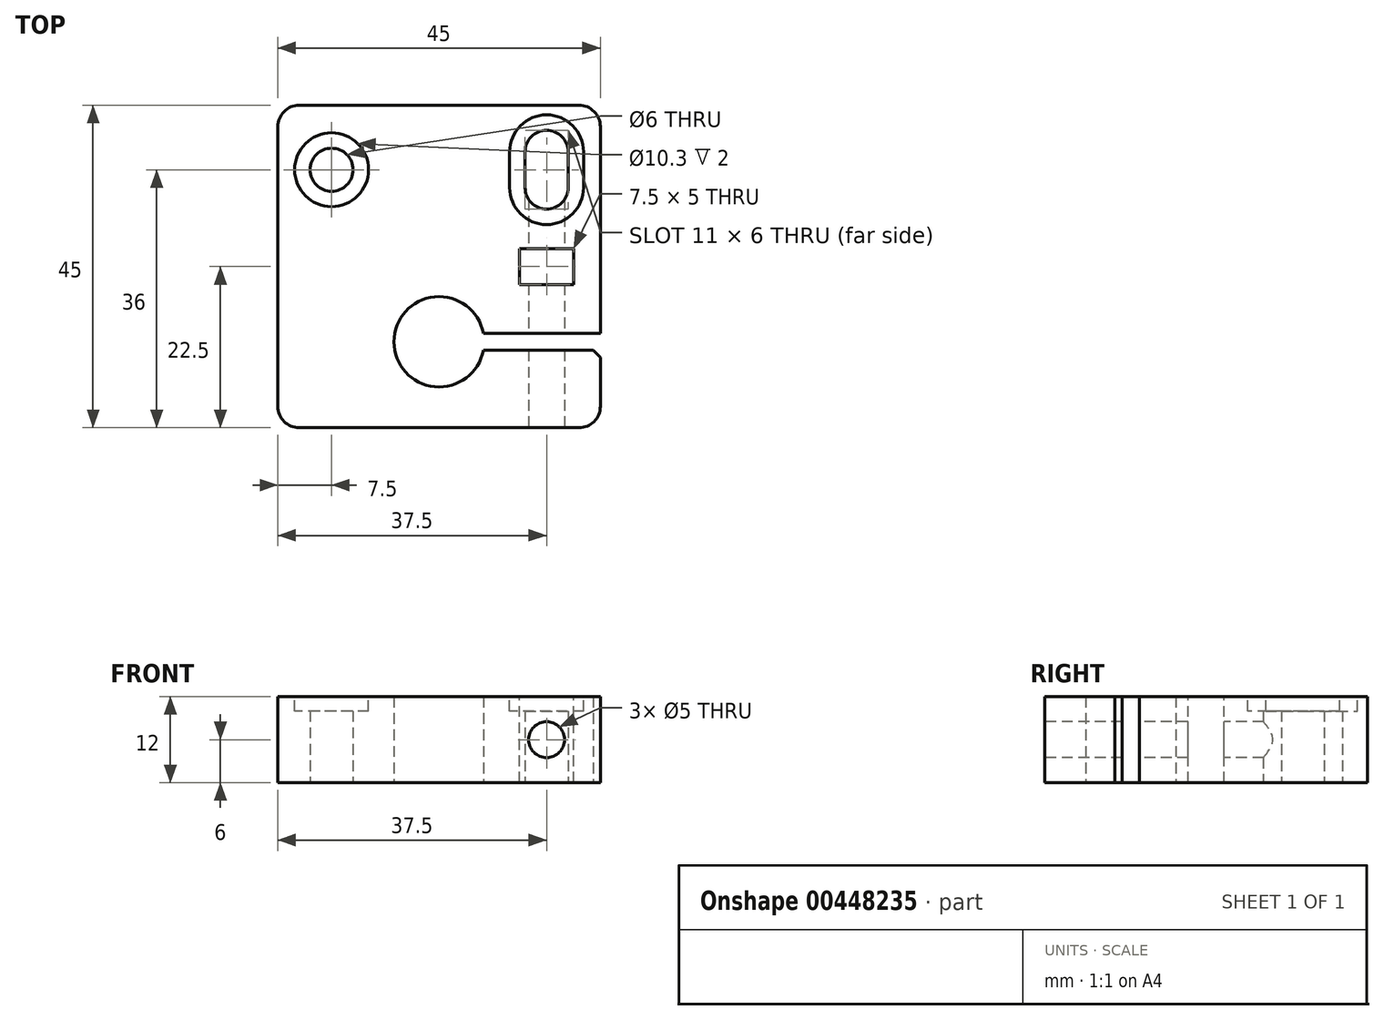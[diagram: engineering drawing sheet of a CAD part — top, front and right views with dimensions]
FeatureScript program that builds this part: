
annotation { "Feature Type Name" : "Feature", "Feature Type Description" : "" }
export const myFeature = defineFeature(function(context is Context, id is Id, definition is map)
    precondition{}
    {
        {
            var Q0;
            Q0=qCreatedBy(makeId("Top.planeOp"),FACE);
            var sketch = newSketch(context, id + "F0", { "sketchPlane" : qUnion([Q0])});
            skLineSegment(sketch, "E0.bottom", {"start": v(-22.5, 33) * mm, "end": v(22.5, 33) * mm});
            skLineSegment(sketch, "E0.top", {"start": v(-22.5, -12) * mm, "end": v(22.5, -12) * mm});
            skLineSegment(sketch, "E0.left", {"start": v(-22.5, 33) * mm, "end": v(-22.5, -12) * mm});
            skLineSegment(sketch, "E0.right", {"start": v(22.5, 33) * mm, "end": v(22.5, -12) * mm});
            skCircle(sketch, "E1", {"center": v(0, 0) * mm, "radius": 6.3 * mm});
            skLineSegment(sketch, "E2", {"start": v(12, 26.5) * mm, "end": v(12, 21.5) * mm});
            skLineSegment(sketch, "E3", {"start": v(12, 21.5) * mm, "end": v(18, 21.5) * mm});
            skLineSegment(sketch, "E4", {"start": v(18, 21.5) * mm, "end": v(18, 26.5) * mm});
            skArc(sketch, "E5", {"start": v(18, 26.5) * mm, "mid": v(15, 29.5) * mm, "end": v(12, 26.5) * mm});
            skArc(sketch, "E6", {"start": v(12, 21.5) * mm, "mid": v(15, 18.5) * mm, "end": v(18, 21.5) * mm});
            skCircle(sketch, "E7", {"center": v(-15, 24) * mm, "radius": 3 * mm});
            skSolve(sketch);
        }
        {
            var Q0;
            Q0=makeQuery(id+"F0.imprint","IMPRINT",FACE,{"disambiguationData":[TD([[makeQuery(id+"F0.imprint","IMPRINT",EDGE,{"derivedFrom":sQuery(id+"F0.wireOp",EDGE,"E0.bottom")}),-1.0]])]});
            extrude(context, id + "F1", {"entities" : qUnion([Q0]), "depth" : 12 * mm});
        }
        {
            var Q0;
            Q0=makeQuery(id+"F1.opExtrude","SWEPT_FACE",FACE,{"disambiguationData":[OSD([sQuery(id+"F0.wireOp",EDGE,"E0.top")])]});
            var sketch = newSketch(context, id + "F2", { "sketchPlane" : qUnion([Q0])});
            skPoint(sketch, "E8", {"position": v(15, 6) * mm});
            skSolve(sketch);
        }
        {
            var Q0;
            Q0=sQuery(id+"F2.wireOp",VERTEX,"E8");
            var Q1;
            Q1=makeQuery(id+"F1.opExtrude","SWEPT_BODY",BODY,{"disambiguationData":[OSD([sQuery(id+"F0.wireOp",EDGE,"E0.bottom"),sQuery(id+"F0.wireOp",EDGE,"E0.top"),sQuery(id+"F0.wireOp",EDGE,"E0.left"),sQuery(id+"F0.wireOp",EDGE,"E0.right"),sQuery(id+"F0.wireOp",EDGE,"E1"),sQuery(id+"F0.wireOp",EDGE,"E2"),sQuery(id+"F0.wireOp",EDGE,"E4"),sQuery(id+"F0.wireOp",EDGE,"E5"),sQuery(id+"F0.wireOp",EDGE,"E6"),sQuery(id+"F0.wireOp",EDGE,"E7")])]});
            hole(context, id + "F3", {"style" : HoleStyle.SIMPLE, "endStyle" : HoleEndStyle.BLIND, "holeDiameter" : 5 * mm, "holeDepth" : 32 * mm, "isTappedThrough" : true, "tappedDepth" : 12 * mm, "tapClearance" : 3, "locations" : qUnion([Q0]), "scope" : qUnion([Q1])});
        }
        {
            var Q0;
            Q0=makeQuery(id+"F1.opExtrude","CAP_FACE",FACE,{"disambiguationData":[OSD([sQuery(id+"F0.wireOp",EDGE,"E0.bottom"),sQuery(id+"F0.wireOp",EDGE,"E0.top"),sQuery(id+"F0.wireOp",EDGE,"E0.left"),sQuery(id+"F0.wireOp",EDGE,"E0.right"),sQuery(id+"F0.wireOp",EDGE,"E1"),sQuery(id+"F0.wireOp",EDGE,"E2"),sQuery(id+"F0.wireOp",EDGE,"E4"),sQuery(id+"F0.wireOp",EDGE,"E5"),sQuery(id+"F0.wireOp",EDGE,"E6"),sQuery(id+"F0.wireOp",EDGE,"E7")])],"isStart":false});
            var sketch = newSketch(context, id + "F4", { "sketchPlane" : qUnion([Q0])});
            skLineSegment(sketch, "E9.bottom", {"start": v(0, 1.2) * mm, "end": v(22.5, 1.2) * mm});
            skLineSegment(sketch, "E9.top", {"start": v(0, -1.2) * mm, "end": v(22.5, -1.2) * mm});
            skLineSegment(sketch, "E9.left", {"start": v(0, 1.2) * mm, "end": v(0, -1.2) * mm});
            skLineSegment(sketch, "E9.right", {"start": v(22.5, 1.2) * mm, "end": v(22.5, -1.2) * mm});
            skSolve(sketch);
        }
        {
            var Q0;
            {var subQ0=sQuery(id+"F4.wireOp",EDGE,"E9.right");Q0=makeQuery(id+"F4.imprint","IMPRINT",FACE,{"disambiguationData":[TD([[makeQuery(id+"F4.imprint","IMPRINT",EDGE,{"derivedFrom":subQ0}),-1.0]])]});}
            var Q1;
            {var subQ0=sQuery(id+"F4.wireOp",EDGE,"E9.left");Q1=makeQuery(id+"F4.imprint","IMPRINT",FACE,{"disambiguationData":[TD([[makeQuery(id+"F4.imprint","IMPRINT",EDGE,{"derivedFrom":subQ0}),1.0]])]});}
            extrude(context, id + "F5", {"entities" : qUnion([Q0, Q1]), "operationType" : NewBodyOperationType.REMOVE, "oppositeDirection" : true, "depth" : 25 * mm});
        }
        {
            var Q0;
            Q0=makeQuery(id+"F1.opExtrude","CAP_FACE",FACE,{"disambiguationData":[OSD([sQuery(id+"F0.wireOp",EDGE,"E0.bottom"),sQuery(id+"F0.wireOp",EDGE,"E0.top"),sQuery(id+"F0.wireOp",EDGE,"E0.left"),sQuery(id+"F0.wireOp",EDGE,"E0.right"),sQuery(id+"F0.wireOp",EDGE,"E1"),sQuery(id+"F0.wireOp",EDGE,"E2"),sQuery(id+"F0.wireOp",EDGE,"E4"),sQuery(id+"F0.wireOp",EDGE,"E5"),sQuery(id+"F0.wireOp",EDGE,"E6"),sQuery(id+"F0.wireOp",EDGE,"E7")])],"isStart":false});
            var sketch = newSketch(context, id + "F6", { "sketchPlane" : qUnion([Q0])});
            skLineSegment(sketch, "E10.bottom", {"start": v(11.25, 13) * mm, "end": v(18.75, 13) * mm});
            skLineSegment(sketch, "E10.top", {"start": v(11.25, 8) * mm, "end": v(18.75, 8) * mm});
            skLineSegment(sketch, "E10.left", {"start": v(11.25, 13) * mm, "end": v(11.25, 8) * mm});
            skLineSegment(sketch, "E10.right", {"start": v(18.75, 13) * mm, "end": v(18.75, 8) * mm});
            skPoint(sketch, "E11", {"position": v(15, 8) * mm});
            skSolve(sketch);
        }
        {
            var Q0;
            Q0=makeQuery(id+"F6.imprint","IMPRINT",FACE,{"disambiguationData":[TD([[makeQuery(id+"F6.imprint","IMPRINT",EDGE,{"derivedFrom":sQuery(id+"F6.wireOp",EDGE,"E10.bottom")}),-1.0]])]});
            extrude(context, id + "F7", {"entities" : qUnion([Q0]), "operationType" : NewBodyOperationType.REMOVE, "oppositeDirection" : true, "depth" : 25 * mm});
        }
        {
            var Q0;
            Q0=makeQuery(id+"F1.opExtrude","SWEPT_EDGE",EDGE,{"disambiguationData":[OSD([sQuery(id+"F0.wireOp",EDGE,"E0.top"),sQuery(id+"F0.wireOp",EDGE,"E0.left")])]});
            var Q1;
            Q1=makeQuery(id+"F1.opExtrude","SWEPT_EDGE",EDGE,{"disambiguationData":[OSD([sQuery(id+"F0.wireOp",EDGE,"E0.top"),sQuery(id+"F0.wireOp",EDGE,"E0.right")])]});
            var Q2;
            Q2=makeQuery(id+"F1.opExtrude","SWEPT_EDGE",EDGE,{"disambiguationData":[OSD([sQuery(id+"F0.wireOp",EDGE,"E0.bottom"),sQuery(id+"F0.wireOp",EDGE,"E0.left")])]});
            var Q3;
            Q3=makeQuery(id+"F1.opExtrude","SWEPT_EDGE",EDGE,{"disambiguationData":[OSD([sQuery(id+"F0.wireOp",EDGE,"E0.bottom"),sQuery(id+"F0.wireOp",EDGE,"E0.right")])]});
            fillet(context, id + "F8", {"entities" : qUnion([Q0, Q1, Q2, Q3]), "radius" : 3 * mm, "tangentPropagation" : true, "allowEdgeOverflow" : false});
        }
        {
            var Q0;
            Q0=makeQuery(id+"F5.boolean.opBoolean","COPY",EDGE,{"derivedFrom":makeQuery(id+"F5.opExtrude","SWEPT_EDGE",EDGE,{"disambiguationData":[OSD([sQuery(id+"F0.wireOp",EDGE,"E0.right"),sQuery(id+"F4.wireOp",EDGE,"E9.top"),sQuery(id+"F4.wireOp",EDGE,"E9.right")])]})});
            var Q1;
            Q1=makeQuery(id+"F5.boolean.opBoolean","COPY",EDGE,{"derivedFrom":makeQuery(id+"F5.opExtrude","SWEPT_EDGE",EDGE,{"disambiguationData":[OSD([sQuery(id+"F0.wireOp",EDGE,"E0.right"),sQuery(id+"F4.wireOp",EDGE,"E9.bottom"),sQuery(id+"F4.wireOp",EDGE,"E9.right")])]})});
            chamfer(context, id + "F9", {"entities" : qUnion([Q0, Q1]), "width" : 1 * mm, "tangentPropagation" : true});
        }
        {
            var Q0;
            Q0=makeQuery(id+"F1.opExtrude","CAP_FACE",FACE,{"disambiguationData":[OSD([sQuery(id+"F0.wireOp",EDGE,"E0.bottom"),sQuery(id+"F0.wireOp",EDGE,"E0.top"),sQuery(id+"F0.wireOp",EDGE,"E0.left"),sQuery(id+"F0.wireOp",EDGE,"E0.right"),sQuery(id+"F0.wireOp",EDGE,"E1"),sQuery(id+"F0.wireOp",EDGE,"E2"),sQuery(id+"F0.wireOp",EDGE,"E4"),sQuery(id+"F0.wireOp",EDGE,"E5"),sQuery(id+"F0.wireOp",EDGE,"E6"),sQuery(id+"F0.wireOp",EDGE,"E7")])],"isStart":false});
            var sketch = newSketch(context, id + "F10", { "sketchPlane" : qUnion([Q0])});
            skCircle(sketch, "E12.0", {"center": v(-15, 24) * mm, "radius": 5.15 * mm});
            skArc(sketch, "E13.0", {"start": v(20.15, 26.5) * mm, "mid": v(15, 31.65) * mm, "end": v(9.85, 26.5) * mm});
            skLineSegment(sketch, "E13.1", {"start": v(20.15, 21.5) * mm, "end": v(20.15, 26.5) * mm});
            skArc(sketch, "E13.2", {"start": v(9.85, 21.5) * mm, "mid": v(15, 16.35) * mm, "end": v(20.15, 21.5) * mm});
            skLineSegment(sketch, "E13.3", {"start": v(9.85, 26.5) * mm, "end": v(9.85, 21.5) * mm});
            skSolve(sketch);
        }
        {
            var Q0;
            Q0=makeQuery(id+"F10.imprint","IMPRINT",FACE,{"disambiguationData":[TD([[makeQuery(id+"F10.imprint","IMPRINT",EDGE,{"derivedFrom":sQuery(id+"F10.wireOp",EDGE,"E12.0")}),1.0]])]});
            var Q1;
            Q1=makeQuery(id+"F10.imprint","IMPRINT",FACE,{"disambiguationData":[TD([[makeQuery(id+"F10.imprint","IMPRINT",EDGE,{"derivedFrom":sQuery(id+"F10.wireOp",EDGE,"E13.0")}),1.0]])]});
            extrude(context, id + "F11", {"entities" : qUnion([Q0, Q1]), "operationType" : NewBodyOperationType.REMOVE, "oppositeDirection" : true, "depth" : 2 * mm});
        }
    });
